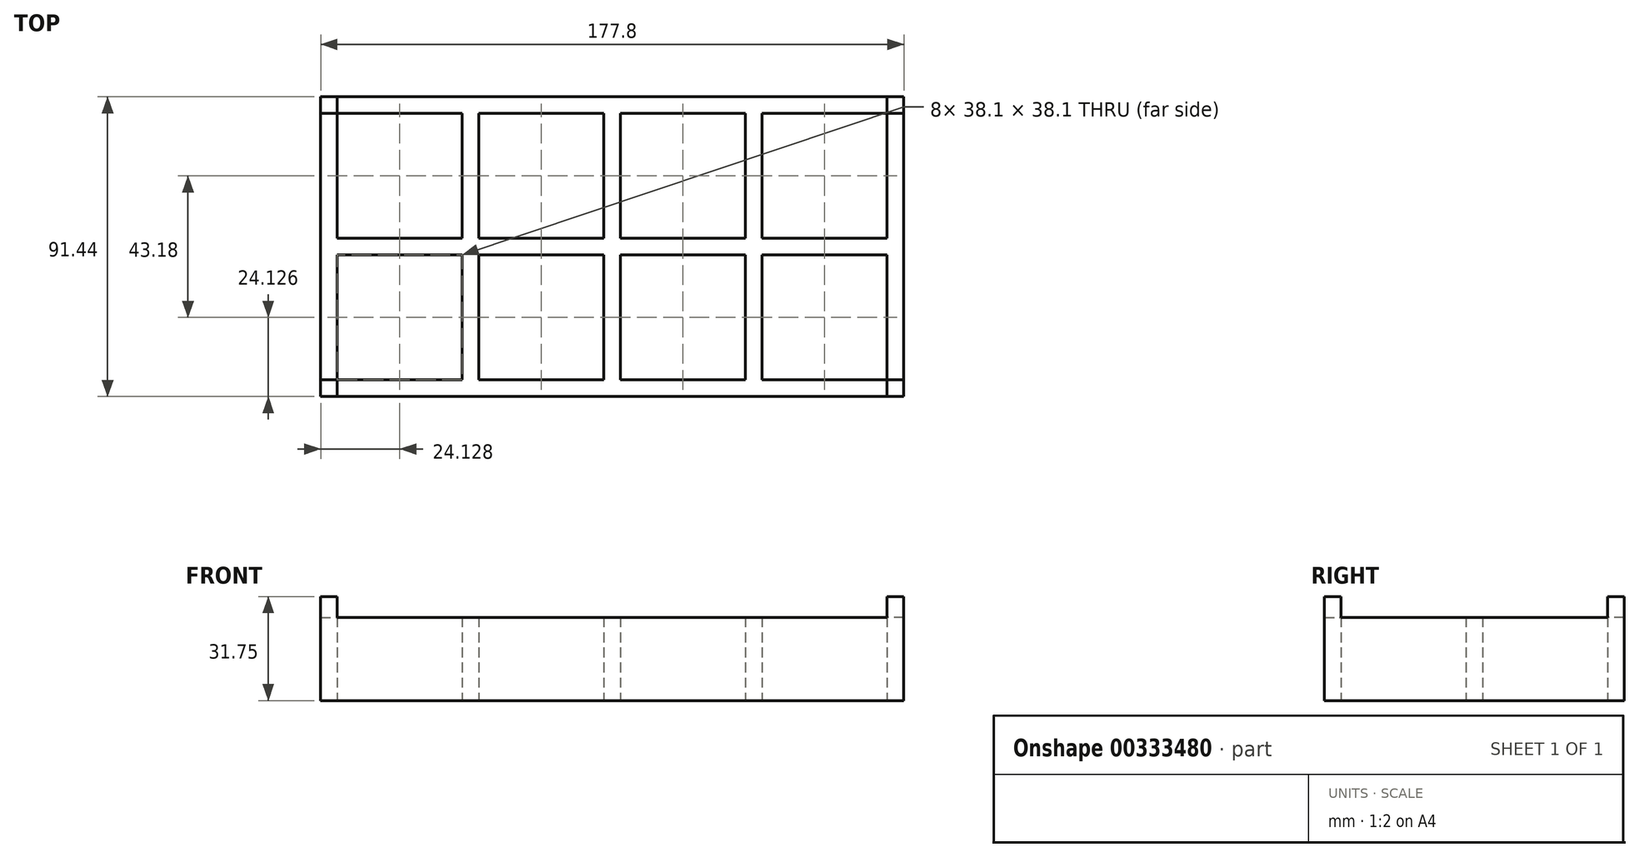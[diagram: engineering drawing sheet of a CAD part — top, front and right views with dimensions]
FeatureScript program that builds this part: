
annotation { "Feature Type Name" : "Feature", "Feature Type Description" : "" }
export const myFeature = defineFeature(function(context is Context, id is Id, definition is map)
    precondition{}
    {
        {
            var Q0;
            Q0=qCreatedBy(makeId("Top.planeOp"),FACE);
            var sketch = newSketch(context, id + "F0", { "sketchPlane" : qUnion([Q0])});
            skLineSegment(sketch, "E0.bottom", {"start": v(-89.84, 9.75) * mm, "end": v(87.96, 9.75) * mm});
            skLineSegment(sketch, "E0.top", {"start": v(-89.84, 101.19) * mm, "end": v(87.96, 101.19) * mm});
            skLineSegment(sketch, "E0.left", {"start": v(-89.84, 9.75) * mm, "end": v(-89.84, 101.19) * mm});
            skLineSegment(sketch, "E0.right", {"start": v(87.96, 9.75) * mm, "end": v(87.96, 101.19) * mm});
            skLineSegment(sketch, "E1.bottom", {"start": v(-84.76, 52.93) * mm, "end": v(-46.66, 52.93) * mm});
            skLineSegment(sketch, "E1.top", {"start": v(-84.76, 14.83) * mm, "end": v(-46.66, 14.83) * mm});
            skLineSegment(sketch, "E1.left", {"start": v(-84.76, 52.93) * mm, "end": v(-84.76, 14.83) * mm});
            skLineSegment(sketch, "E1.right", {"start": v(-46.66, 52.93) * mm, "end": v(-46.66, 14.83) * mm});
            skLineSegment(sketch, "E2.0.1.0", {"start": v(-46.66, 96.1) * mm, "end": v(-46.66, 58) * mm});
            skLineSegment(sketch, "E2.0.1.1", {"start": v(-84.76, 96.1) * mm, "end": v(-46.66, 96.1) * mm});
            skLineSegment(sketch, "E2.0.1.2", {"start": v(-84.76, 96.1) * mm, "end": v(-84.76, 58) * mm});
            skLineSegment(sketch, "E2.0.1.3", {"start": v(-84.76, 58) * mm, "end": v(-46.66, 58) * mm});
            skLineSegment(sketch, "E2.1.0.0", {"start": v(-3.48, 52.93) * mm, "end": v(-3.48, 14.83) * mm});
            skLineSegment(sketch, "E2.1.0.1", {"start": v(-41.58, 52.93) * mm, "end": v(-3.48, 52.93) * mm});
            skLineSegment(sketch, "E2.1.0.2", {"start": v(-41.58, 52.93) * mm, "end": v(-41.58, 14.83) * mm});
            skLineSegment(sketch, "E2.1.0.3", {"start": v(-41.58, 14.83) * mm, "end": v(-3.48, 14.83) * mm});
            skLineSegment(sketch, "E2.1.1.0", {"start": v(-3.48, 96.1) * mm, "end": v(-3.48, 58) * mm});
            skLineSegment(sketch, "E2.1.1.1", {"start": v(-41.58, 96.1) * mm, "end": v(-3.48, 96.1) * mm});
            skLineSegment(sketch, "E2.1.1.2", {"start": v(-41.58, 96.1) * mm, "end": v(-41.58, 58) * mm});
            skLineSegment(sketch, "E2.1.1.3", {"start": v(-41.58, 58) * mm, "end": v(-3.48, 58) * mm});
            skLineSegment(sketch, "E2.2.0.0", {"start": v(39.7, 52.93) * mm, "end": v(39.7, 14.83) * mm});
            skLineSegment(sketch, "E2.2.0.1", {"start": v(1.6, 52.93) * mm, "end": v(39.7, 52.93) * mm});
            skLineSegment(sketch, "E2.2.0.2", {"start": v(1.6, 52.93) * mm, "end": v(1.6, 14.83) * mm});
            skLineSegment(sketch, "E2.2.0.3", {"start": v(1.6, 14.83) * mm, "end": v(39.7, 14.83) * mm});
            skLineSegment(sketch, "E2.2.1.0", {"start": v(39.7, 96.1) * mm, "end": v(39.7, 58) * mm});
            skLineSegment(sketch, "E2.2.1.1", {"start": v(1.6, 96.1) * mm, "end": v(39.7, 96.1) * mm});
            skLineSegment(sketch, "E2.2.1.2", {"start": v(1.6, 96.1) * mm, "end": v(1.6, 58) * mm});
            skLineSegment(sketch, "E2.2.1.3", {"start": v(1.6, 58) * mm, "end": v(39.7, 58) * mm});
            skLineSegment(sketch, "E2.3.0.0", {"start": v(82.88, 52.93) * mm, "end": v(82.88, 14.83) * mm});
            skLineSegment(sketch, "E2.3.0.1", {"start": v(44.78, 52.93) * mm, "end": v(82.88, 52.93) * mm});
            skLineSegment(sketch, "E2.3.0.2", {"start": v(44.78, 52.93) * mm, "end": v(44.78, 14.83) * mm});
            skLineSegment(sketch, "E2.3.0.3", {"start": v(44.78, 14.83) * mm, "end": v(82.88, 14.83) * mm});
            skLineSegment(sketch, "E2.3.1.0", {"start": v(82.88, 96.1) * mm, "end": v(82.88, 58) * mm});
            skLineSegment(sketch, "E2.3.1.1", {"start": v(44.78, 96.1) * mm, "end": v(82.88, 96.1) * mm});
            skLineSegment(sketch, "E2.3.1.2", {"start": v(44.78, 96.1) * mm, "end": v(44.78, 58) * mm});
            skLineSegment(sketch, "E2.3.1.3", {"start": v(44.78, 58) * mm, "end": v(82.88, 58) * mm});
            skLineSegment(sketch, "E2.direction1", {"start": v(-46.66, 14.83) * mm, "end": v(-3.48, 14.83) * mm, "construction": true});
            skLineSegment(sketch, "E2.direction2", {"start": v(-46.66, 14.83) * mm, "end": v(-46.66, 58) * mm, "construction": true});
            skSolve(sketch);
        }
        {
            var Q0;
            Q0 = qSketchRegion(id + "F0", true);
            extrude(context, id + "F1", {"entities" : qUnion([Q0]), "depth" : 25.4 * mm});
        }
        {
            var Q0;
            Q0=makeQuery(id+"F1.opExtrude","CAP_FACE",FACE,{"disambiguationData":[OSD([sQuery(id+"F0.wireOp",EDGE,"E0.bottom"),sQuery(id+"F0.wireOp",EDGE,"E0.top"),sQuery(id+"F0.wireOp",EDGE,"E0.left"),sQuery(id+"F0.wireOp",EDGE,"E0.right"),sQuery(id+"F0.wireOp",EDGE,"E1.bottom"),sQuery(id+"F0.wireOp",EDGE,"E1.top"),sQuery(id+"F0.wireOp",EDGE,"E1.left"),sQuery(id+"F0.wireOp",EDGE,"E1.right"),sQuery(id+"F0.wireOp",EDGE,"E2.0.1.0"),sQuery(id+"F0.wireOp",EDGE,"E2.0.1.1"),sQuery(id+"F0.wireOp",EDGE,"E2.0.1.2"),sQuery(id+"F0.wireOp",EDGE,"E2.0.1.3"),sQuery(id+"F0.wireOp",EDGE,"E2.1.0.0"),sQuery(id+"F0.wireOp",EDGE,"E2.1.0.1"),sQuery(id+"F0.wireOp",EDGE,"E2.1.0.2"),sQuery(id+"F0.wireOp",EDGE,"E2.1.0.3"),sQuery(id+"F0.wireOp",EDGE,"E2.1.1.0"),sQuery(id+"F0.wireOp",EDGE,"E2.1.1.1"),sQuery(id+"F0.wireOp",EDGE,"E2.1.1.2"),sQuery(id+"F0.wireOp",EDGE,"E2.1.1.3"),sQuery(id+"F0.wireOp",EDGE,"E2.2.0.0"),sQuery(id+"F0.wireOp",EDGE,"E2.2.0.1"),sQuery(id+"F0.wireOp",EDGE,"E2.2.0.2"),sQuery(id+"F0.wireOp",EDGE,"E2.2.0.3"),sQuery(id+"F0.wireOp",EDGE,"E2.2.1.0"),sQuery(id+"F0.wireOp",EDGE,"E2.2.1.1"),sQuery(id+"F0.wireOp",EDGE,"E2.2.1.2"),sQuery(id+"F0.wireOp",EDGE,"E2.2.1.3"),sQuery(id+"F0.wireOp",EDGE,"E2.3.0.0"),sQuery(id+"F0.wireOp",EDGE,"E2.3.0.1"),sQuery(id+"F0.wireOp",EDGE,"E2.3.0.2"),sQuery(id+"F0.wireOp",EDGE,"E2.3.0.3"),sQuery(id+"F0.wireOp",EDGE,"E2.3.1.0"),sQuery(id+"F0.wireOp",EDGE,"E2.3.1.1"),sQuery(id+"F0.wireOp",EDGE,"E2.3.1.2"),sQuery(id+"F0.wireOp",EDGE,"E2.3.1.3"),sQuery(id+"F0.wireOp",EDGE,"E2.4.0.0"),sQuery(id+"F0.wireOp",EDGE,"E2.4.0.1"),sQuery(id+"F0.wireOp",EDGE,"E2.4.0.2"),sQuery(id+"F0.wireOp",EDGE,"E2.4.0.3"),sQuery(id+"F0.wireOp",EDGE,"E2.4.1.0"),sQuery(id+"F0.wireOp",EDGE,"E2.4.1.1"),sQuery(id+"F0.wireOp",EDGE,"E2.4.1.2"),sQuery(id+"F0.wireOp",EDGE,"E2.4.1.3")])],"isStart":false});
            var sketch = newSketch(context, id + "F2", { "sketchPlane" : qUnion([Q0])});
            skLineSegment(sketch, "E3.bottom", {"start": v(-89.84, 101.19) * mm, "end": v(-84.76, 101.19) * mm});
            skLineSegment(sketch, "E3.top", {"start": v(-89.84, 96.1) * mm, "end": v(-84.76, 96.1) * mm});
            skLineSegment(sketch, "E3.left", {"start": v(-89.84, 101.19) * mm, "end": v(-89.84, 96.1) * mm});
            skLineSegment(sketch, "E3.right", {"start": v(-84.76, 101.19) * mm, "end": v(-84.76, 96.1) * mm});
            skLineSegment(sketch, "E4.bottom", {"start": v(-89.84, 9.75) * mm, "end": v(-84.76, 9.75) * mm});
            skLineSegment(sketch, "E4.top", {"start": v(-89.84, 14.83) * mm, "end": v(-84.76, 14.83) * mm});
            skLineSegment(sketch, "E4.left", {"start": v(-89.84, 9.75) * mm, "end": v(-89.84, 14.83) * mm});
            skLineSegment(sketch, "E4.right", {"start": v(-84.76, 9.75) * mm, "end": v(-84.76, 14.83) * mm});
            skLineSegment(sketch, "E5.bottom", {"start": v(87.96, 9.75) * mm, "end": v(82.88, 9.75) * mm});
            skLineSegment(sketch, "E5.top", {"start": v(87.96, 14.83) * mm, "end": v(82.88, 14.83) * mm});
            skLineSegment(sketch, "E5.left", {"start": v(87.96, 9.75) * mm, "end": v(87.96, 14.83) * mm});
            skLineSegment(sketch, "E5.right", {"start": v(82.88, 9.75) * mm, "end": v(82.88, 14.83) * mm});
            skLineSegment(sketch, "E6.bottom", {"start": v(87.96, 101.19) * mm, "end": v(82.88, 101.19) * mm});
            skLineSegment(sketch, "E6.top", {"start": v(87.96, 96.1) * mm, "end": v(82.88, 96.1) * mm});
            skLineSegment(sketch, "E6.left", {"start": v(87.96, 101.19) * mm, "end": v(87.96, 96.1) * mm});
            skLineSegment(sketch, "E6.right", {"start": v(82.88, 101.19) * mm, "end": v(82.88, 96.1) * mm});
            skSolve(sketch);
        }
        {
            var Q0;
            Q0 = qSketchRegion(id + "F2", true);
            extrude(context, id + "F3", {"entities" : qUnion([Q0]), "operationType" : NewBodyOperationType.ADD, "depth" : 6.35 * mm});
        }
    });
